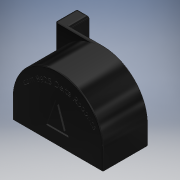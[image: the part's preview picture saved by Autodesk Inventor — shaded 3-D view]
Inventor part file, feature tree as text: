
AUTODESK INVENTOR PART (.ipt)
format: ipt  version: 2019 (Build 230136000, 136)  size: 867,840 bytes
history: native  units: mm (DEFAULTED — no unit token found)
features: sketch x10, extrude x9, fillet x2, shell x1, hole x1, projected_geometry x1
ambient origin geometry x8: Origin, YZ Plane, XZ Plane, XY Plane, X Axis, Y Axis, Z Axis, Center Point
bodies: Body1 (feature_tree)
feature tree (24):
  extrude  "Extrusion2"  Depth=44.45mm TaperAngle=0.0deg
  shell  "Shell2"  Thickness=3.175mm
  extrude  "Extrusion3"  Depth=3.175mm TaperAngle=0.0deg
  extrude  "Extrusion4"  Depth=19.05mm TaperAngle=0.0deg
  extrude  "Extrusion6"  Depth=9.525mm TaperAngle=0.0deg
  extrude  "Extrusion7"  Depth=6.35mm
  extrude  "Extrusion8"  Depth=6.35mm
  hole  "Hole2"  [1 undecoded]
  extrude  "Extrusion9"  Depth=9.525mm TaperAngle=0.0deg
  fillet  "Fillet1"  Radius=3.175mm
  fillet  "Fillet2"  Radius=1.27mm
  extrude  "Extrusion10"  Depth=25.4mm
  extrude  "Extrusion12"  Depth=38.1mm
  sketch  "Sketch2"  dims[d3=88.9mm d7=44.45mm d8=0.0mm d9=3.175mm]
  sketch  "Sketch3"  dims[d10=3.175mm d11=0.0mm d12=3.175mm d13=0.0mm]
  sketch  "Sketch4"  dims[d19=19.05mm d20=0.0mm d21=19.05mm d22=0.0mm]
  sketch  "Sketch8"  dims[d35=12.7mm d36=9.525mm d37=0.0mm]
  projected_geometry  "Projected Loop2"
  sketch  "Sketch9"  dims[d38=16.764mm d39=6.35mm]
  sketch  "Sketch12"  dims[d40=6.35mm d41=6.35mm]
  sketch  "Sketch13"  dims[d42=3.81mm d43=19.05mm d44=9.525mm d45=6.35mm d46=90.0deg d47=25.4mm d48=20.594885mm d49=9.525mm]
  sketch  "Sketch14"  dims[d50=12.7mm d51=9.525mm d52=0.0mm d53=3.175mm d54=1.27mm]
  sketch  "Sketch15"  dims[d55=25.4mm d56=25.4mm]
  sketch  "Sketch16"  dims[d57=12.7mm d58=38.1mm d59=1.5875mm d60=0.0mm d64=0.0mm d65=1.5875mm d66=0.0mm]
note: 1 required parameter value undecoded (feature->parameter linkage not recoverable at this tier; creation-order binding heuristic only, values carry confidence <= 0.55)
